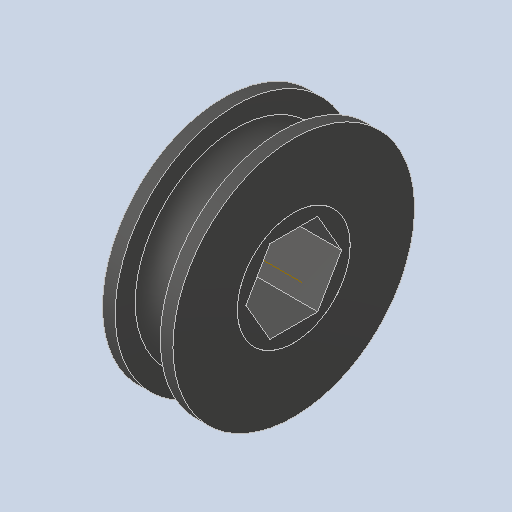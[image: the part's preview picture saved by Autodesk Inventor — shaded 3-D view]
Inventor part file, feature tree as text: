
AUTODESK INVENTOR PART (.ipt)
format: ipt  version: 2022.3 (Build 263350000, 350)  size: 184,832 bytes
history: native  units: in
note: dims shown in document units (in); Inventor stores cm internally (conversion verified against a paired STEP export)
features: thicken_offset x3, other x1, fillet x1
ambient origin geometry x8: Origin, YZ Plane, XZ Plane, XY Plane, X Axis, Y Axis, Z Axis, Center Point
bodies: Solid1 (feature_tree)
feature tree (5):
  thicken_offset  "Thicken1"
  thicken_offset  "Thicken2"
  thicken_offset  "Thicken3"
  other  "Work Axis1"
  fillet  "Fillet1"  Radius=0.015in
